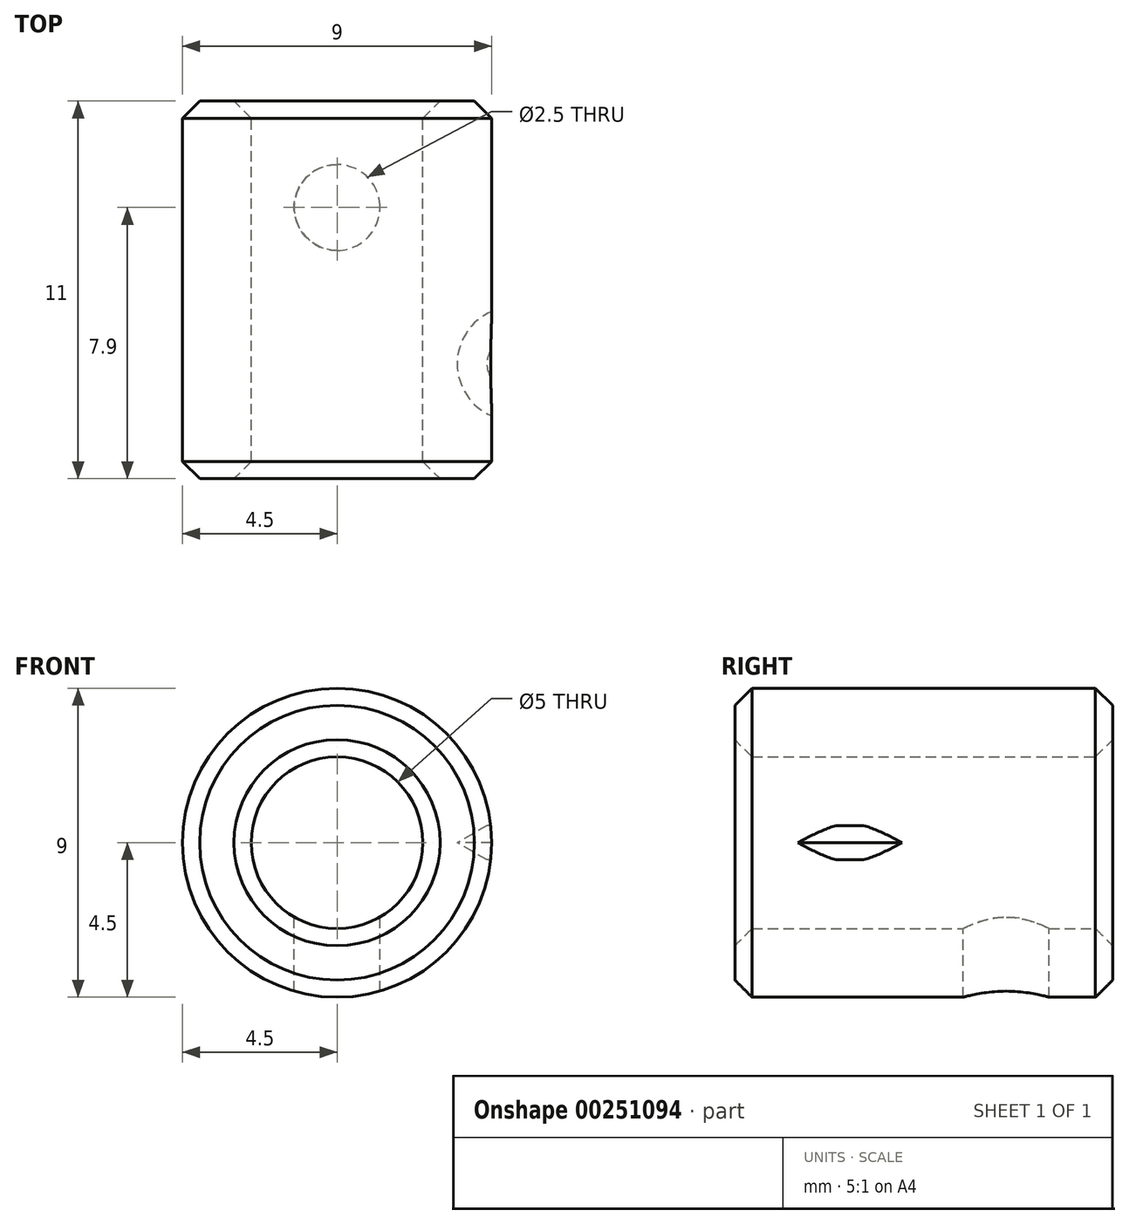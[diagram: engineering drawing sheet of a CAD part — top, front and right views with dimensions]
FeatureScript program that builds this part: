
annotation { "Feature Type Name" : "Feature", "Feature Type Description" : "" }
export const myFeature = defineFeature(function(context is Context, id is Id, definition is map)
    precondition{}
    {
        {
            var Q0;
            Q0=qCreatedBy(makeId("Front.planeOp"),FACE);
            var sketch = newSketch(context, id + "F0", { "sketchPlane" : qUnion([Q0])});
            skCircle(sketch, "E0", {"center": v(0, 0) * mm, "radius": 4.5 * mm});
            skCircle(sketch, "E1", {"center": v(0, 0) * mm, "radius": 2.5 * mm});
            skSolve(sketch);
        }
        {
            var Q0;
            Q0 = qSketchRegion(id + "F0", true);
            extrude(context, id + "F1", {"entities" : qUnion([Q0]), "depth" : 11 * mm});
        }
        {
            var Q0;
            Q0=qCreatedBy(makeId("Top.planeOp"),FACE);
            var sketch = newSketch(context, id + "F2", { "sketchPlane" : qUnion([Q0])});
            skCircle(sketch, "E2", {"center": v(5.15, -7.65) * mm, "radius": 1.65 * mm});
            skLineSegment(sketch, "E3", {"start": v(0, -26.8) * mm, "end": v(0, 9.04) * mm, "construction": true});
            skSolve(sketch);
        }
        {
            var Q0;
            Q0 = qSketchRegion(id + "F2", true);
            extrude(context, id + "F3", {"entities" : qUnion([Q0]), "endBound" : BoundingType.SYMMETRIC, "depth" : 1 * mm, "hasDraft" : true, "draftAngle" : 60 * degree, "draftPullDirection" : true});
        }
        {
            var Q0;
            Q0=makeQuery(id+"FlCykohCmPU6IM3_2.11.F3.*.split.splitOp","SPLIT",BODY,{"derivedFrom":makeQuery(id+"FlCykohCmPU6IM3_2.11.F3.opExtrude","SWEPT_BODY",BODY,{"disambiguationData":[OSD([sQuery(id+"F2.wireOp",EDGE,"E2")])]})});
            var Q1;
            Q1=makeQuery(id+"FlCykohCmPU6IM3_2.2.F3.*.split.splitOp","SPLIT",BODY,{"derivedFrom":makeQuery(id+"FlCykohCmPU6IM3_2.2.F3.opExtrude","SWEPT_BODY",BODY,{"disambiguationData":[OSD([sQuery(id+"F2.wireOp",EDGE,"E2")])]})});
            var Q2;
            Q2=makeQuery(id+"FlCykohCmPU6IM3_2.1.F3.*.split.splitOp","SPLIT",BODY,{"derivedFrom":makeQuery(id+"FlCykohCmPU6IM3_2.1.F3.opExtrude","SWEPT_BODY",BODY,{"disambiguationData":[OSD([sQuery(id+"F2.wireOp",EDGE,"E2")])]})});
            var Q3;
            Q3=makeQuery(id+"FlCykohCmPU6IM3_2.10.F3.*.split.splitOp","SPLIT",BODY,{"derivedFrom":makeQuery(id+"FlCykohCmPU6IM3_2.10.F3.opExtrude","SWEPT_BODY",BODY,{"disambiguationData":[OSD([sQuery(id+"F2.wireOp",EDGE,"E2")])]})});
            var Q4;
            Q4=makeQuery(id+"FlCykohCmPU6IM3_2.13.F3.*.split.splitOp","SPLIT",BODY,{"derivedFrom":makeQuery(id+"FlCykohCmPU6IM3_2.13.F3.opExtrude","SWEPT_BODY",BODY,{"disambiguationData":[OSD([sQuery(id+"F2.wireOp",EDGE,"E2")])]})});
            var Q5;
            Q5=makeQuery(id+"FlCykohCmPU6IM3_2.5.F3.*.split.splitOp","SPLIT",BODY,{"derivedFrom":makeQuery(id+"FlCykohCmPU6IM3_2.5.F3.opExtrude","SWEPT_BODY",BODY,{"disambiguationData":[OSD([sQuery(id+"F2.wireOp",EDGE,"E2")])]})});
            var Q6;
            Q6=makeQuery(id+"FlCykohCmPU6IM3_2.9.F3.*.split.splitOp","SPLIT",BODY,{"derivedFrom":makeQuery(id+"FlCykohCmPU6IM3_2.9.F3.opExtrude","SWEPT_BODY",BODY,{"disambiguationData":[OSD([sQuery(id+"F2.wireOp",EDGE,"E2")])]})});
            var Q7;
            Q7=makeQuery(id+"FlCykohCmPU6IM3_2.6.F3.*.split.splitOp","SPLIT",BODY,{"derivedFrom":makeQuery(id+"FlCykohCmPU6IM3_2.6.F3.opExtrude","SWEPT_BODY",BODY,{"disambiguationData":[OSD([sQuery(id+"F2.wireOp",EDGE,"E2")])]})});
            var Q8;
            Q8=makeQuery(id+"FlCykohCmPU6IM3_2.14.F3.*.split.splitOp","SPLIT",BODY,{"derivedFrom":makeQuery(id+"FlCykohCmPU6IM3_2.14.F3.opExtrude","SWEPT_BODY",BODY,{"disambiguationData":[OSD([sQuery(id+"F2.wireOp",EDGE,"E2")])]})});
            var Q9;
            Q9=makeQuery(id+"FlCykohCmPU6IM3_2.19.F3.*.split.splitOp","SPLIT",BODY,{"derivedFrom":makeQuery(id+"FlCykohCmPU6IM3_2.19.F3.opExtrude","SWEPT_BODY",BODY,{"disambiguationData":[OSD([sQuery(id+"F2.wireOp",EDGE,"E2")])]})});
            var Q10;
            Q10=makeQuery(id+"FlCykohCmPU6IM3_2.4.F3.*.split.splitOp","SPLIT",BODY,{"derivedFrom":makeQuery(id+"FlCykohCmPU6IM3_2.4.F3.opExtrude","SWEPT_BODY",BODY,{"disambiguationData":[OSD([sQuery(id+"F2.wireOp",EDGE,"E2")])]})});
            var Q11;
            Q11=makeQuery(id+"F3.*.split.splitOp","SPLIT",BODY,{"derivedFrom":makeQuery(id+"F3.opExtrude","SWEPT_BODY",BODY,{"disambiguationData":[OSD([sQuery(id+"F2.wireOp",EDGE,"E2")])]})});
            var Q12;
            Q12=makeQuery(id+"FlCykohCmPU6IM3_2.3.F3.*.split.splitOp","SPLIT",BODY,{"derivedFrom":makeQuery(id+"FlCykohCmPU6IM3_2.3.F3.opExtrude","SWEPT_BODY",BODY,{"disambiguationData":[OSD([sQuery(id+"F2.wireOp",EDGE,"E2")])]})});
            var Q13;
            Q13=makeQuery(id+"FlCykohCmPU6IM3_2.7.F3.*.split.splitOp","SPLIT",BODY,{"derivedFrom":makeQuery(id+"FlCykohCmPU6IM3_2.7.F3.opExtrude","SWEPT_BODY",BODY,{"disambiguationData":[OSD([sQuery(id+"F2.wireOp",EDGE,"E2")])]})});
            var Q14;
            Q14=makeQuery(id+"FlCykohCmPU6IM3_2.33.F3.*.split.splitOp","SPLIT",BODY,{"derivedFrom":makeQuery(id+"FlCykohCmPU6IM3_2.33.F3.opExtrude","SWEPT_BODY",BODY,{"disambiguationData":[OSD([sQuery(id+"F2.wireOp",EDGE,"E2")])]})});
            var Q15;
            Q15=makeQuery(id+"FlCykohCmPU6IM3_2.32.F3.*.split.splitOp","SPLIT",BODY,{"derivedFrom":makeQuery(id+"FlCykohCmPU6IM3_2.32.F3.opExtrude","SWEPT_BODY",BODY,{"disambiguationData":[OSD([sQuery(id+"F2.wireOp",EDGE,"E2")])]})});
            var Q16;
            Q16=makeQuery(id+"FlCykohCmPU6IM3_2.31.F3.*.split.splitOp","SPLIT",BODY,{"derivedFrom":makeQuery(id+"FlCykohCmPU6IM3_2.31.F3.opExtrude","SWEPT_BODY",BODY,{"disambiguationData":[OSD([sQuery(id+"F2.wireOp",EDGE,"E2")])]})});
            var Q17;
            Q17=makeQuery(id+"FlCykohCmPU6IM3_2.30.F3.*.split.splitOp","SPLIT",BODY,{"derivedFrom":makeQuery(id+"FlCykohCmPU6IM3_2.30.F3.opExtrude","SWEPT_BODY",BODY,{"disambiguationData":[OSD([sQuery(id+"F2.wireOp",EDGE,"E2")])]})});
            var Q18;
            Q18=makeQuery(id+"FlCykohCmPU6IM3_2.29.F3.*.split.splitOp","SPLIT",BODY,{"derivedFrom":makeQuery(id+"FlCykohCmPU6IM3_2.29.F3.opExtrude","SWEPT_BODY",BODY,{"disambiguationData":[OSD([sQuery(id+"F2.wireOp",EDGE,"E2")])]})});
            var Q19;
            Q19=makeQuery(id+"FlCykohCmPU6IM3_2.28.F3.*.split.splitOp","SPLIT",BODY,{"derivedFrom":makeQuery(id+"FlCykohCmPU6IM3_2.28.F3.opExtrude","SWEPT_BODY",BODY,{"disambiguationData":[OSD([sQuery(id+"F2.wireOp",EDGE,"E2")])]})});
            var Q20;
            Q20=makeQuery(id+"FlCykohCmPU6IM3_2.27.F3.*.split.splitOp","SPLIT",BODY,{"derivedFrom":makeQuery(id+"FlCykohCmPU6IM3_2.27.F3.opExtrude","SWEPT_BODY",BODY,{"disambiguationData":[OSD([sQuery(id+"F2.wireOp",EDGE,"E2")])]})});
            var Q21;
            Q21=makeQuery(id+"FlCykohCmPU6IM3_2.26.F3.*.split.splitOp","SPLIT",BODY,{"derivedFrom":makeQuery(id+"FlCykohCmPU6IM3_2.26.F3.opExtrude","SWEPT_BODY",BODY,{"disambiguationData":[OSD([sQuery(id+"F2.wireOp",EDGE,"E2")])]})});
            var Q22;
            Q22=makeQuery(id+"FlCykohCmPU6IM3_2.25.F3.*.split.splitOp","SPLIT",BODY,{"derivedFrom":makeQuery(id+"FlCykohCmPU6IM3_2.25.F3.opExtrude","SWEPT_BODY",BODY,{"disambiguationData":[OSD([sQuery(id+"F2.wireOp",EDGE,"E2")])]})});
            var Q23;
            Q23=makeQuery(id+"FlCykohCmPU6IM3_2.24.F3.*.split.splitOp","SPLIT",BODY,{"derivedFrom":makeQuery(id+"FlCykohCmPU6IM3_2.24.F3.opExtrude","SWEPT_BODY",BODY,{"disambiguationData":[OSD([sQuery(id+"F2.wireOp",EDGE,"E2")])]})});
            var Q24;
            Q24=makeQuery(id+"FlCykohCmPU6IM3_2.23.F3.*.split.splitOp","SPLIT",BODY,{"derivedFrom":makeQuery(id+"FlCykohCmPU6IM3_2.23.F3.opExtrude","SWEPT_BODY",BODY,{"disambiguationData":[OSD([sQuery(id+"F2.wireOp",EDGE,"E2")])]})});
            var Q25;
            Q25=makeQuery(id+"FlCykohCmPU6IM3_2.22.F3.*.split.splitOp","SPLIT",BODY,{"derivedFrom":makeQuery(id+"FlCykohCmPU6IM3_2.22.F3.opExtrude","SWEPT_BODY",BODY,{"disambiguationData":[OSD([sQuery(id+"F2.wireOp",EDGE,"E2")])]})});
            var Q26;
            Q26=makeQuery(id+"FlCykohCmPU6IM3_2.21.F3.*.split.splitOp","SPLIT",BODY,{"derivedFrom":makeQuery(id+"FlCykohCmPU6IM3_2.21.F3.opExtrude","SWEPT_BODY",BODY,{"disambiguationData":[OSD([sQuery(id+"F2.wireOp",EDGE,"E2")])]})});
            var Q27;
            Q27=makeQuery(id+"FlCykohCmPU6IM3_2.20.F3.*.split.splitOp","SPLIT",BODY,{"derivedFrom":makeQuery(id+"FlCykohCmPU6IM3_2.20.F3.opExtrude","SWEPT_BODY",BODY,{"disambiguationData":[OSD([sQuery(id+"F2.wireOp",EDGE,"E2")])]})});
            var Q28;
            Q28=makeQuery(id+"FlCykohCmPU6IM3_2.12.F3.*.split.splitOp","SPLIT",BODY,{"derivedFrom":makeQuery(id+"FlCykohCmPU6IM3_2.12.F3.opExtrude","SWEPT_BODY",BODY,{"disambiguationData":[OSD([sQuery(id+"F2.wireOp",EDGE,"E2")])]})});
            var Q29;
            Q29=makeQuery(id+"FlCykohCmPU6IM3_2.8.F3.*.split.splitOp","SPLIT",BODY,{"derivedFrom":makeQuery(id+"FlCykohCmPU6IM3_2.8.F3.opExtrude","SWEPT_BODY",BODY,{"disambiguationData":[OSD([sQuery(id+"F2.wireOp",EDGE,"E2")])]})});
            var Q30;
            Q30=makeQuery(id+"FlCykohCmPU6IM3_2.16.F3.*.split.splitOp","SPLIT",BODY,{"derivedFrom":makeQuery(id+"FlCykohCmPU6IM3_2.16.F3.opExtrude","SWEPT_BODY",BODY,{"disambiguationData":[OSD([sQuery(id+"F2.wireOp",EDGE,"E2")])]})});
            var Q31;
            Q31=makeQuery(id+"FlCykohCmPU6IM3_2.15.F3.*.split.splitOp","SPLIT",BODY,{"derivedFrom":makeQuery(id+"FlCykohCmPU6IM3_2.15.F3.opExtrude","SWEPT_BODY",BODY,{"disambiguationData":[OSD([sQuery(id+"F2.wireOp",EDGE,"E2")])]})});
            var Q32;
            Q32=makeQuery(id+"FlCykohCmPU6IM3_2.17.F3.*.split.splitOp","SPLIT",BODY,{"derivedFrom":makeQuery(id+"FlCykohCmPU6IM3_2.17.F3.opExtrude","SWEPT_BODY",BODY,{"disambiguationData":[OSD([sQuery(id+"F2.wireOp",EDGE,"E2")])]})});
            var Q33;
            Q33=makeQuery(id+"FlCykohCmPU6IM3_2.18.F3.*.split.splitOp","SPLIT",BODY,{"derivedFrom":makeQuery(id+"FlCykohCmPU6IM3_2.18.F3.opExtrude","SWEPT_BODY",BODY,{"disambiguationData":[OSD([sQuery(id+"F2.wireOp",EDGE,"E2")])]})});
            var Q34;
            Q34=makeQuery(id+"FlCykohCmPU6IM3_2.34.F3.*.split.splitOp","SPLIT",BODY,{"derivedFrom":makeQuery(id+"FlCykohCmPU6IM3_2.34.F3.opExtrude","SWEPT_BODY",BODY,{"disambiguationData":[OSD([sQuery(id+"F2.wireOp",EDGE,"E2")])]})});
            var Q35;
            Q35=makeQuery(id+"FlCykohCmPU6IM3_2.47.F3.*.split.splitOp","SPLIT",BODY,{"derivedFrom":makeQuery(id+"FlCykohCmPU6IM3_2.47.F3.opExtrude","SWEPT_BODY",BODY,{"disambiguationData":[OSD([sQuery(id+"F2.wireOp",EDGE,"E2")])]})});
            var Q36;
            Q36=makeQuery(id+"FlCykohCmPU6IM3_2.35.F3.*.split.splitOp","SPLIT",BODY,{"derivedFrom":makeQuery(id+"FlCykohCmPU6IM3_2.35.F3.opExtrude","SWEPT_BODY",BODY,{"disambiguationData":[OSD([sQuery(id+"F2.wireOp",EDGE,"E2")])]})});
            var Q37;
            Q37=makeQuery(id+"FlCykohCmPU6IM3_2.40.F3.*.split.splitOp","SPLIT",BODY,{"derivedFrom":makeQuery(id+"FlCykohCmPU6IM3_2.40.F3.opExtrude","SWEPT_BODY",BODY,{"disambiguationData":[OSD([sQuery(id+"F2.wireOp",EDGE,"E2")])]})});
            var Q38;
            Q38=makeQuery(id+"FlCykohCmPU6IM3_2.42.F3.*.split.splitOp","SPLIT",BODY,{"derivedFrom":makeQuery(id+"FlCykohCmPU6IM3_2.42.F3.opExtrude","SWEPT_BODY",BODY,{"disambiguationData":[OSD([sQuery(id+"F2.wireOp",EDGE,"E2")])]})});
            var Q39;
            Q39=makeQuery(id+"FlCykohCmPU6IM3_2.39.F3.*.split.splitOp","SPLIT",BODY,{"derivedFrom":makeQuery(id+"FlCykohCmPU6IM3_2.39.F3.opExtrude","SWEPT_BODY",BODY,{"disambiguationData":[OSD([sQuery(id+"F2.wireOp",EDGE,"E2")])]})});
            var Q40;
            Q40=makeQuery(id+"FlCykohCmPU6IM3_2.44.F3.*.split.splitOp","SPLIT",BODY,{"derivedFrom":makeQuery(id+"FlCykohCmPU6IM3_2.44.F3.opExtrude","SWEPT_BODY",BODY,{"disambiguationData":[OSD([sQuery(id+"F2.wireOp",EDGE,"E2")])]})});
            var Q41;
            Q41=makeQuery(id+"FlCykohCmPU6IM3_2.46.F3.*.split.splitOp","SPLIT",BODY,{"derivedFrom":makeQuery(id+"FlCykohCmPU6IM3_2.46.F3.opExtrude","SWEPT_BODY",BODY,{"disambiguationData":[OSD([sQuery(id+"F2.wireOp",EDGE,"E2")])]})});
            var Q42;
            Q42=makeQuery(id+"FlCykohCmPU6IM3_2.45.F3.*.split.splitOp","SPLIT",BODY,{"derivedFrom":makeQuery(id+"FlCykohCmPU6IM3_2.45.F3.opExtrude","SWEPT_BODY",BODY,{"disambiguationData":[OSD([sQuery(id+"F2.wireOp",EDGE,"E2")])]})});
            var Q43;
            Q43=makeQuery(id+"FlCykohCmPU6IM3_2.38.F3.*.split.splitOp","SPLIT",BODY,{"derivedFrom":makeQuery(id+"FlCykohCmPU6IM3_2.38.F3.opExtrude","SWEPT_BODY",BODY,{"disambiguationData":[OSD([sQuery(id+"F2.wireOp",EDGE,"E2")])]})});
            var Q44;
            Q44=makeQuery(id+"FlCykohCmPU6IM3_2.36.F3.*.split.splitOp","SPLIT",BODY,{"derivedFrom":makeQuery(id+"FlCykohCmPU6IM3_2.36.F3.opExtrude","SWEPT_BODY",BODY,{"disambiguationData":[OSD([sQuery(id+"F2.wireOp",EDGE,"E2")])]})});
            var Q45;
            Q45=makeQuery(id+"FlCykohCmPU6IM3_2.37.F3.*.split.splitOp","SPLIT",BODY,{"derivedFrom":makeQuery(id+"FlCykohCmPU6IM3_2.37.F3.opExtrude","SWEPT_BODY",BODY,{"disambiguationData":[OSD([sQuery(id+"F2.wireOp",EDGE,"E2")])]})});
            var Q46;
            Q46=makeQuery(id+"FlCykohCmPU6IM3_2.48.F3.*.split.splitOp","SPLIT",BODY,{"derivedFrom":makeQuery(id+"FlCykohCmPU6IM3_2.48.F3.opExtrude","SWEPT_BODY",BODY,{"disambiguationData":[OSD([sQuery(id+"F2.wireOp",EDGE,"E2")])]})});
            var Q47;
            Q47=makeQuery(id+"FlCykohCmPU6IM3_2.41.F3.*.split.splitOp","SPLIT",BODY,{"derivedFrom":makeQuery(id+"FlCykohCmPU6IM3_2.41.F3.opExtrude","SWEPT_BODY",BODY,{"disambiguationData":[OSD([sQuery(id+"F2.wireOp",EDGE,"E2")])]})});
            var Q48;
            Q48=makeQuery(id+"FlCykohCmPU6IM3_2.43.F3.*.split.splitOp","SPLIT",BODY,{"derivedFrom":makeQuery(id+"FlCykohCmPU6IM3_2.43.F3.opExtrude","SWEPT_BODY",BODY,{"disambiguationData":[OSD([sQuery(id+"F2.wireOp",EDGE,"E2")])]})});
            var Q49;
            Q49=makeQuery(id+"FlCykohCmPU6IM3_2.59.F3.*.split.splitOp","SPLIT",BODY,{"derivedFrom":makeQuery(id+"FlCykohCmPU6IM3_2.59.F3.opExtrude","SWEPT_BODY",BODY,{"disambiguationData":[OSD([sQuery(id+"F2.wireOp",EDGE,"E2")])]})});
            var Q50;
            Q50=makeQuery(id+"FlCykohCmPU6IM3_2.58.F3.*.split.splitOp","SPLIT",BODY,{"derivedFrom":makeQuery(id+"FlCykohCmPU6IM3_2.58.F3.opExtrude","SWEPT_BODY",BODY,{"disambiguationData":[OSD([sQuery(id+"F2.wireOp",EDGE,"E2")])]})});
            var Q51;
            Q51=makeQuery(id+"FlCykohCmPU6IM3_2.57.F3.*.split.splitOp","SPLIT",BODY,{"derivedFrom":makeQuery(id+"FlCykohCmPU6IM3_2.57.F3.opExtrude","SWEPT_BODY",BODY,{"disambiguationData":[OSD([sQuery(id+"F2.wireOp",EDGE,"E2")])]})});
            var Q52;
            Q52=makeQuery(id+"FlCykohCmPU6IM3_2.56.F3.*.split.splitOp","SPLIT",BODY,{"derivedFrom":makeQuery(id+"FlCykohCmPU6IM3_2.56.F3.opExtrude","SWEPT_BODY",BODY,{"disambiguationData":[OSD([sQuery(id+"F2.wireOp",EDGE,"E2")])]})});
            var Q53;
            Q53=makeQuery(id+"FlCykohCmPU6IM3_2.55.F3.*.split.splitOp","SPLIT",BODY,{"derivedFrom":makeQuery(id+"FlCykohCmPU6IM3_2.55.F3.opExtrude","SWEPT_BODY",BODY,{"disambiguationData":[OSD([sQuery(id+"F2.wireOp",EDGE,"E2")])]})});
            var Q54;
            Q54=makeQuery(id+"FlCykohCmPU6IM3_2.54.F3.*.split.splitOp","SPLIT",BODY,{"derivedFrom":makeQuery(id+"FlCykohCmPU6IM3_2.54.F3.opExtrude","SWEPT_BODY",BODY,{"disambiguationData":[OSD([sQuery(id+"F2.wireOp",EDGE,"E2")])]})});
            var Q55;
            Q55=makeQuery(id+"FlCykohCmPU6IM3_2.53.F3.*.split.splitOp","SPLIT",BODY,{"derivedFrom":makeQuery(id+"FlCykohCmPU6IM3_2.53.F3.opExtrude","SWEPT_BODY",BODY,{"disambiguationData":[OSD([sQuery(id+"F2.wireOp",EDGE,"E2")])]})});
            var Q56;
            Q56=makeQuery(id+"FlCykohCmPU6IM3_2.52.F3.*.split.splitOp","SPLIT",BODY,{"derivedFrom":makeQuery(id+"FlCykohCmPU6IM3_2.52.F3.opExtrude","SWEPT_BODY",BODY,{"disambiguationData":[OSD([sQuery(id+"F2.wireOp",EDGE,"E2")])]})});
            var Q57;
            Q57=makeQuery(id+"FlCykohCmPU6IM3_2.51.F3.*.split.splitOp","SPLIT",BODY,{"derivedFrom":makeQuery(id+"FlCykohCmPU6IM3_2.51.F3.opExtrude","SWEPT_BODY",BODY,{"disambiguationData":[OSD([sQuery(id+"F2.wireOp",EDGE,"E2")])]})});
            var Q58;
            Q58=makeQuery(id+"FlCykohCmPU6IM3_2.50.F3.*.split.splitOp","SPLIT",BODY,{"derivedFrom":makeQuery(id+"FlCykohCmPU6IM3_2.50.F3.opExtrude","SWEPT_BODY",BODY,{"disambiguationData":[OSD([sQuery(id+"F2.wireOp",EDGE,"E2")])]})});
            var Q59;
            Q59=makeQuery(id+"FlCykohCmPU6IM3_2.49.F3.*.split.splitOp","SPLIT",BODY,{"derivedFrom":makeQuery(id+"FlCykohCmPU6IM3_2.49.F3.opExtrude","SWEPT_BODY",BODY,{"disambiguationData":[OSD([sQuery(id+"F2.wireOp",EDGE,"E2")])]})});
            var Q60;
            Q60=makeQuery(id+"F1.opExtrude","SWEPT_BODY",BODY,{"disambiguationData":[OSD([sQuery(id+"F0.wireOp",EDGE,"E0"),sQuery(id+"F0.wireOp",EDGE,"E1")])]});
            booleanBodies(context, id + "F4", {"operationType" : BooleanOperationType.SUBTRACTION, "tools" : qUnion([Q0, Q1, Q2, Q3, Q4, Q5, Q6, Q7, Q8, Q9, Q10, Q11, Q12, Q13, Q14, Q15, Q16, Q17, Q18, Q19, Q20, Q21, Q22, Q23, Q24, Q25, Q26, Q27, Q28, Q29, Q30, Q31, Q32, Q33, Q34, Q35, Q36, Q37, Q38, Q39, Q40, Q41, Q42, Q43, Q44, Q45, Q46, Q47, Q48, Q49, Q50, Q51, Q52, Q53, Q54, Q55, Q56, Q57, Q58, Q59]), "targets" : qUnion([Q60])});
        }
        {
            var Q0;
            Q0=qCreatedBy(makeId("Top.planeOp"),FACE);
            var sketch = newSketch(context, id + "F5", { "sketchPlane" : qUnion([Q0])});
            skCircle(sketch, "E4", {"center": v(0, -3.1) * mm, "radius": 1.25 * mm});
            skSolve(sketch);
        }
        {
            var Q0;
            Q0 = qSketchRegion(id + "F5", true);
            var Q1;
            {var subQ0=sQuery(id+"F0.wireOp",EDGE,"E0");Q1=makeQuery(id+"FioVggKPFHV3JOt_1.boolean.opBoolean","SPLIT",FACE,{"disambiguationData":[TD([makeQuery(id+"F1.opExtrude","CAP_FACE",FACE,{"disambiguationData":[OSD([subQ0,sQuery(id+"F0.wireOp",EDGE,"E1")])],"isStart":true})])],"derivedFrom":makeQuery(id+"F1.opExtrude","SWEPT_FACE",FACE,{"disambiguationData":[OSD([subQ0])]})});}
            extrude(context, id + "F6", {"entities" : qUnion([Q0]), "operationType" : NewBodyOperationType.REMOVE, "endBound" : BoundingType.UP_TO_SURFACE, "oppositeDirection" : true, "endBoundEntityFace" : qUnion([Q1]), "depth" : 25 * mm});
        }
        {
            var Q0;
            Q0=makeQuery(id+"F1.opExtrude","CAP_EDGE",EDGE,{"disambiguationData":[OSD([sQuery(id+"F0.wireOp",EDGE,"E0")])],"isStart":false});
            var Q1;
            Q1=makeQuery(id+"F1.opExtrude","CAP_EDGE",EDGE,{"disambiguationData":[OSD([sQuery(id+"F0.wireOp",EDGE,"E1")])],"isStart":false});
            var Q2;
            Q2=makeQuery(id+"F1.opExtrude","CAP_EDGE",EDGE,{"disambiguationData":[OSD([sQuery(id+"F0.wireOp",EDGE,"E1")])],"isStart":true});
            var Q3;
            Q3=makeQuery(id+"F1.opExtrude","CAP_EDGE",EDGE,{"disambiguationData":[OSD([sQuery(id+"F0.wireOp",EDGE,"E0")])],"isStart":true});
            chamfer(context, id + "F7", {"entities" : qUnion([Q0, Q1, Q2, Q3]), "width" : .5 * mm, "tangentPropagation" : true});
        }
    });
